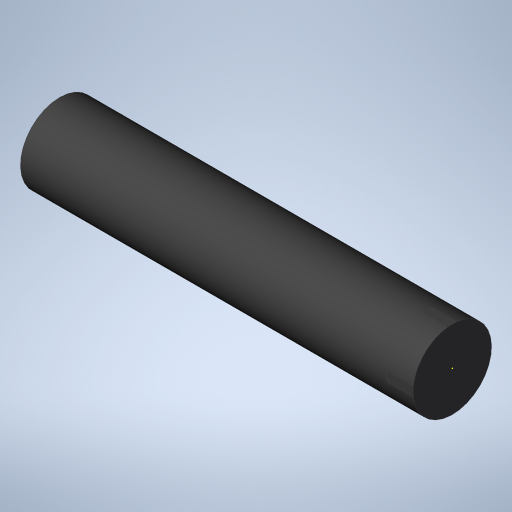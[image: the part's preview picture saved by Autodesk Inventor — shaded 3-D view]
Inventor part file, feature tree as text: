
AUTODESK INVENTOR PART (.ipt)
format: ipt  version: 2024.3 (Build 283343000, 343)  size: 240,640 bytes
history: native  units: mm
features: sketch x4, extrude x3, projected_geometry x1
ambient origin geometry x8: Origin, YZ Plane, XZ Plane, XY Plane, X Axis, Y Axis, Z Axis, Center Point
bodies: Solid1 (feature_tree)
feature tree (8):
  extrude  "Extrusion1"  Depth=15.0mm TaperAngle=0.0deg
  extrude  "Extrusion2"  Depth=1.0mm TaperAngle=0.0deg
  sketch  "Sketch3"  dims[d6=1.49mm d7=1.0mm d8=0.0mm]
  extrude  "Extrusion3"  Depth=1.0mm TaperAngle=0.0deg
  sketch  "Sketch1"  dims[d0=3.0mm d1=15.0mm d2=0.0mm]
  sketch  "Sketch2"  dims[d3=1.49mm d4=1.0mm d5=0.0mm]
  projected_geometry  "Projected Loop1"
  sketch  "Sketch4"
